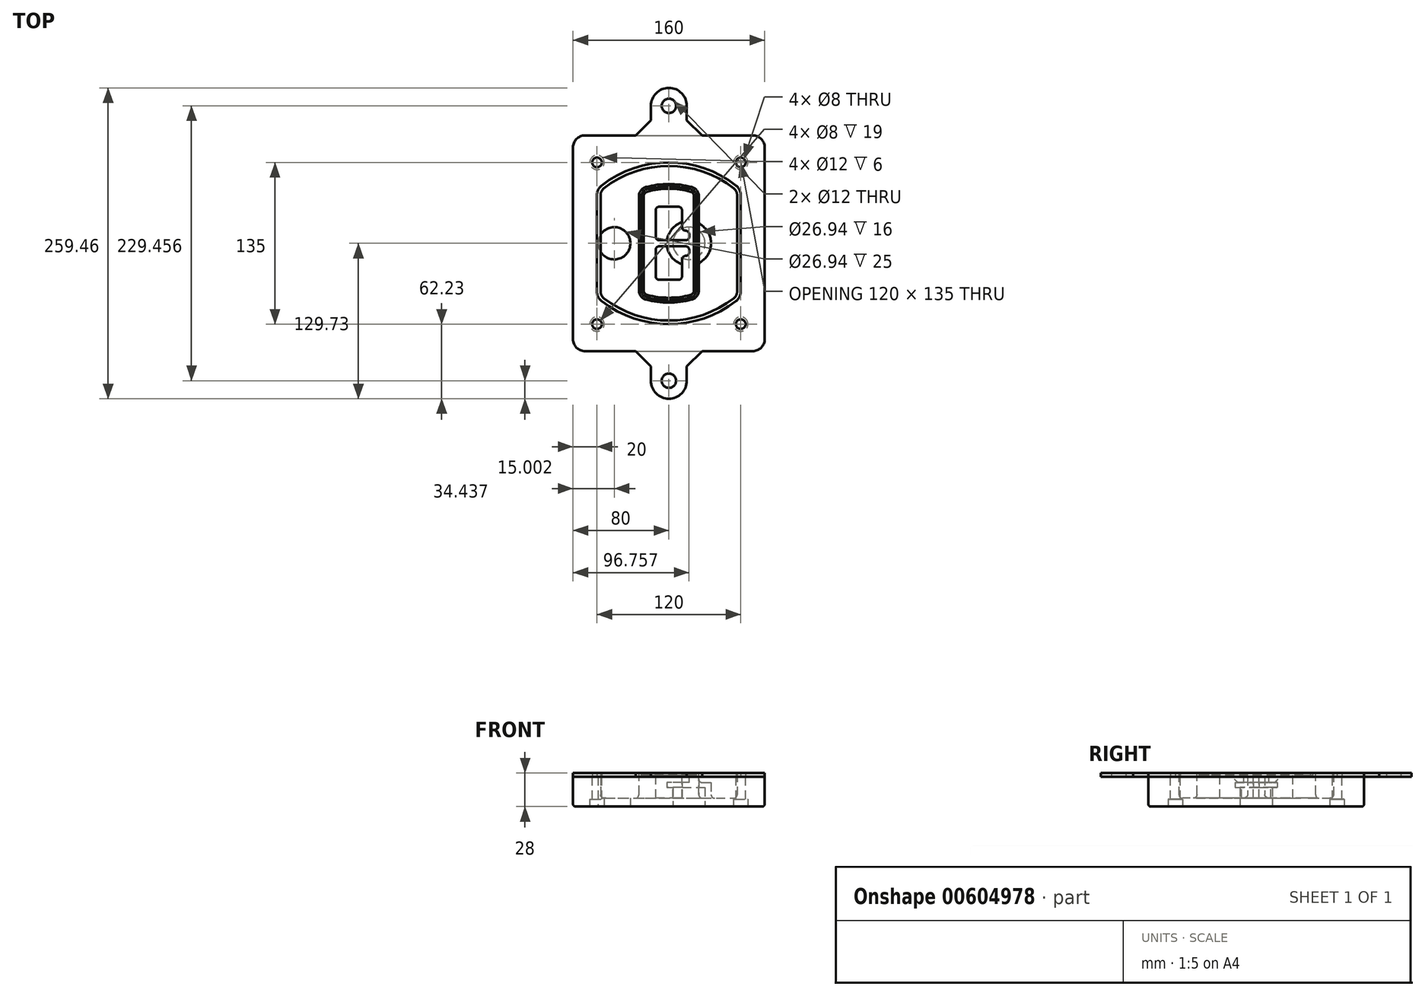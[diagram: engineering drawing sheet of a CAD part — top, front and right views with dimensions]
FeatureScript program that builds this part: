
annotation { "Feature Type Name" : "Feature", "Feature Type Description" : "" }
export const myFeature = defineFeature(function(context is Context, id is Id, definition is map)
    precondition{}
    {
        {
            var Q0;
            Q0=qCreatedBy(makeId("Top.planeOp"),FACE);
            var sketch = newSketch(context, id + "F0", { "sketchPlane" : qUnion([Q0])});
            skPoint(sketch, "E0.rect.middle", {"position": v(0, 0) * mm});
            skLineSegment(sketch, "E1.bottom", {"start": v(-70, -90) * mm, "end": v(70, -90) * mm});
            skLineSegment(sketch, "E1.top", {"start": v(-70, 90) * mm, "end": v(70, 90) * mm});
            skLineSegment(sketch, "E1.left", {"start": v(-80, -80) * mm, "end": v(-80, 80) * mm});
            skLineSegment(sketch, "E1.right", {"start": v(80, -80) * mm, "end": v(80, 80) * mm});
            skLineSegment(sketch, "E2", {"start": v(-80, 90) * mm, "end": v(80, -90) * mm, "construction": true});
            skLineSegment(sketch, "E3", {"start": v(80, 90) * mm, "end": v(-80, -90) * mm, "construction": true});
            skCircle(sketch, "E4", {"center": v(-60, 67.5) * mm, "radius": 4 * mm});
            skCircle(sketch, "E5", {"center": v(60, 67.5) * mm, "radius": 4 * mm});
            skCircle(sketch, "E6", {"center": v(60, -67.5) * mm, "radius": 4 * mm});
            skCircle(sketch, "E7", {"center": v(-60, -67.5) * mm, "radius": 4 * mm});
            skLineSegment(sketch, "E8", {"start": v(-60, 67.5) * mm, "end": v(60, 67.5) * mm, "construction": true});
            skLineSegment(sketch, "E9", {"start": v(60, 67.5) * mm, "end": v(60, -67.5) * mm, "construction": true});
            skLineSegment(sketch, "E10", {"start": v(60, -67.5) * mm, "end": v(-60, -67.5) * mm, "construction": true});
            skLineSegment(sketch, "E11", {"start": v(-60, -67.5) * mm, "end": v(-60, 67.5) * mm, "construction": true});
            skLineSegment(sketch, "E12", {"start": v(-60, 40.3) * mm, "end": v(-60, -40.3) * mm});
            skLineSegment(sketch, "E13", {"start": v(60, 40.3) * mm, "end": v(60, -40.3) * mm});
            skArc(sketch, "E14", {"start": v(56.15, 48.18) * mm, "mid": v(0, 67.5) * mm, "end": v(-56.15, 48.18) * mm});
            skArc(sketch, "E15", {"start": v(-56.15, -48.18) * mm, "mid": v(0, -67.5) * mm, "end": v(56.15, -48.18) * mm});
            skLineSegment(sketch, "E16", {"start": v(-60, 0) * mm, "end": v(60, 0) * mm, "construction": true});
            skPoint(sketch, "E17.visualSharp", {"position": v(-60, -45) * mm});
            skArc(sketch, "E17.filletArc", {"start": v(-60, -40.3) * mm, "mid": v(-58.99, -44.68) * mm, "end": v(-56.15, -48.18) * mm});
            skPoint(sketch, "E18.visualSharp", {"position": v(-60, 45) * mm});
            skArc(sketch, "E18.filletArc", {"start": v(-56.15, 48.18) * mm, "mid": v(-58.99, 44.68) * mm, "end": v(-60, 40.3) * mm});
            skPoint(sketch, "E19.visualSharp", {"position": v(60, 45) * mm});
            skArc(sketch, "E19.filletArc", {"start": v(60, 40.3) * mm, "mid": v(58.99, 44.68) * mm, "end": v(56.15, 48.18) * mm});
            skPoint(sketch, "E20.visualSharp", {"position": v(60, -45) * mm});
            skArc(sketch, "E20.filletArc", {"start": v(56.15, -48.18) * mm, "mid": v(58.99, -44.68) * mm, "end": v(60, -40.3) * mm});
            skPoint(sketch, "E21.visualSharp", {"position": v(-80, 90) * mm});
            skArc(sketch, "E21.filletArc", {"start": v(-70, 90) * mm, "mid": v(-77.07, 87.07) * mm, "end": v(-80, 80) * mm});
            skPoint(sketch, "E22.visualSharp", {"position": v(80, 90) * mm});
            skArc(sketch, "E22.filletArc", {"start": v(80, 80) * mm, "mid": v(77.07, 87.07) * mm, "end": v(70, 90) * mm});
            skPoint(sketch, "E23.visualSharp", {"position": v(80, -90) * mm});
            skArc(sketch, "E23.filletArc", {"start": v(70, -90) * mm, "mid": v(77.07, -87.07) * mm, "end": v(80, -80) * mm});
            skPoint(sketch, "E24.visualSharp", {"position": v(-80, -90) * mm});
            skArc(sketch, "E24.filletArc", {"start": v(-80, -80) * mm, "mid": v(-77.07, -87.07) * mm, "end": v(-70, -90) * mm});
            skArc(sketch, "E25.0", {"start": v(57, 40.3) * mm, "mid": v(56.3, 43.36) * mm, "end": v(54.3, 45.81) * mm});
            skLineSegment(sketch, "E25.1", {"start": v(57, 40.3) * mm, "end": v(57, -40.3) * mm});
            skArc(sketch, "E25.2", {"start": v(54.3, -45.81) * mm, "mid": v(56.3, -43.36) * mm, "end": v(57, -40.3) * mm});
            skArc(sketch, "E25.3", {"start": v(-54.3, -45.81) * mm, "mid": v(0, -64.5) * mm, "end": v(54.3, -45.81) * mm});
            skArc(sketch, "E25.4", {"start": v(-57, -40.3) * mm, "mid": v(-56.3, -43.36) * mm, "end": v(-54.3, -45.81) * mm});
            skArc(sketch, "E25.5", {"start": v(54.3, 45.81) * mm, "mid": v(0, 64.5) * mm, "end": v(-54.3, 45.81) * mm});
            skLineSegment(sketch, "E25.6", {"start": v(-57, 40.3) * mm, "end": v(-57, -40.3) * mm});
            skArc(sketch, "E25.7", {"start": v(-54.3, 45.81) * mm, "mid": v(-56.3, 43.36) * mm, "end": v(-57, 40.3) * mm});
            skArc(sketch, "E26.0", {"start": v(-58.62, 51.33) * mm, "mid": v(-62.58, 46.43) * mm, "end": v(-64, 40.3) * mm});
            skArc(sketch, "E26.1", {"start": v(58.62, 51.33) * mm, "mid": v(0, 71.5) * mm, "end": v(-58.62, 51.33) * mm});
            skArc(sketch, "E26.2", {"start": v(64, 40.3) * mm, "mid": v(62.58, 46.43) * mm, "end": v(58.62, 51.33) * mm});
            skLineSegment(sketch, "E26.3", {"start": v(64, 40.3) * mm, "end": v(64, -40.3) * mm});
            skArc(sketch, "E26.4", {"start": v(58.62, -51.33) * mm, "mid": v(62.58, -46.43) * mm, "end": v(64, -40.3) * mm});
            skLineSegment(sketch, "E26.5", {"start": v(-64, 40.3) * mm, "end": v(-64, -40.3) * mm});
            skArc(sketch, "E26.6", {"start": v(-58.62, -51.33) * mm, "mid": v(0, -71.5) * mm, "end": v(58.62, -51.33) * mm});
            skArc(sketch, "E26.7", {"start": v(-64, -40.3) * mm, "mid": v(-62.58, -46.43) * mm, "end": v(-58.62, -51.33) * mm});
            skSolve(sketch);
        }
        {
            var Q0;
            Q0=makeQuery(id+"F0.imprint","IMPRINT",FACE,{"disambiguationData":[TD([[makeQuery(id+"F0.imprint","IMPRINT",EDGE,{"derivedFrom":sQuery(id+"F0.wireOp",EDGE,"E1.bottom")}),1.0]])]});
            var Q1;
            Q1=makeQuery(id+"F0.imprint","IMPRINT",FACE,{"disambiguationData":[TD([[makeQuery(id+"F0.imprint","IMPRINT",EDGE,{"derivedFrom":sQuery(id+"F0.wireOp",EDGE,"E12")}),1.0]])]});
            var Q2;
            Q2=makeQuery(id+"F0.imprint","IMPRINT",FACE,{"disambiguationData":[TD([[makeQuery(id+"F0.imprint","IMPRINT",EDGE,{"derivedFrom":sQuery(id+"F0.wireOp",EDGE,"E25.0")}),1.0]])]});
            var Q3;
            Q3=makeQuery(id+"F0.imprint","IMPRINT",FACE,{"disambiguationData":[TD([[makeQuery(id+"F0.imprint","IMPRINT",EDGE,{"derivedFrom":sQuery(id+"F0.wireOp",EDGE,"E12")}),-1.0]])]});
            extrude(context, id + "F1", {"entities" : qUnion([Q0, Q1, Q2, Q3]), "oppositeDirection" : true, "depth" : 25 * mm});
        }
        {
            var Q0;
            Q0=makeQuery(id+"F0.imprint","IMPRINT",FACE,{"disambiguationData":[TD([[makeQuery(id+"F0.imprint","IMPRINT",EDGE,{"derivedFrom":sQuery(id+"F0.wireOp",EDGE,"E12")}),1.0]])]});
            extrude(context, id + "F2", {"entities" : qUnion([Q0]), "operationType" : NewBodyOperationType.ADD, "depth" : 3 * mm});
        }
        {
            var Q0;
            Q0=makeQuery(id+"F0.imprint","IMPRINT",FACE,{"disambiguationData":[TD([[makeQuery(id+"F0.imprint","IMPRINT",EDGE,{"derivedFrom":sQuery(id+"F0.wireOp",EDGE,"E25.0")}),1.0]])]});
            extrude(context, id + "F3", {"entities" : qUnion([Q0]), "operationType" : NewBodyOperationType.REMOVE, "oppositeDirection" : true, "depth" : 18 * mm});
        }
        {
            var Q0;
            Q0=makeQuery(id+"F2.opExtrude","CAP_FACE",FACE,{"disambiguationData":[OSD([sQuery(id+"F0.wireOp",EDGE,"E12"),sQuery(id+"F0.wireOp",EDGE,"E13"),sQuery(id+"F0.wireOp",EDGE,"E14"),sQuery(id+"F0.wireOp",EDGE,"E15"),sQuery(id+"F0.wireOp",EDGE,"E17.filletArc"),sQuery(id+"F0.wireOp",EDGE,"E18.filletArc"),sQuery(id+"F0.wireOp",EDGE,"E19.filletArc"),sQuery(id+"F0.wireOp",EDGE,"E20.filletArc"),sQuery(id+"F0.wireOp",EDGE,"E25.0"),sQuery(id+"F0.wireOp",EDGE,"E25.1"),sQuery(id+"F0.wireOp",EDGE,"E25.2"),sQuery(id+"F0.wireOp",EDGE,"E25.3"),sQuery(id+"F0.wireOp",EDGE,"E25.4"),sQuery(id+"F0.wireOp",EDGE,"E25.5"),sQuery(id+"F0.wireOp",EDGE,"E25.6"),sQuery(id+"F0.wireOp",EDGE,"E25.7")])],"isStart":false});
            var sketch = newSketch(context, id + "F4", { "sketchPlane" : qUnion([Q0])});
            skArc(sketch, "E27.0", {"start": v(-19.08, -46.97) * mm, "mid": v(0, -49.5) * mm, "end": v(19.08, -46.97) * mm});
            skArc(sketch, "E28.0", {"start": v(19.08, 46.97) * mm, "mid": v(0, 49.5) * mm, "end": v(-19.08, 46.97) * mm});
            skLineSegment(sketch, "E29", {"start": v(-25, 39.25) * mm, "end": v(-25, -39.25) * mm});
            skLineSegment(sketch, "E30", {"start": v(25, 39.25) * mm, "end": v(25, -39.25) * mm});
            skLineSegment(sketch, "E31", {"start": v(-25, 45.1) * mm, "end": v(25, 45.1) * mm, "construction": true});
            skLineSegment(sketch, "E32", {"start": v(-25, -45.1) * mm, "end": v(25, -45.1) * mm, "construction": true});
            skPoint(sketch, "E33.visualSharp", {"position": v(-25, 45.1) * mm});
            skArc(sketch, "E33.filletArc", {"start": v(-19.08, 46.97) * mm, "mid": v(-23.35, 44.11) * mm, "end": v(-25, 39.25) * mm});
            skPoint(sketch, "E34.visualSharp", {"position": v(25, 45.1) * mm});
            skArc(sketch, "E34.filletArc", {"start": v(25, 39.25) * mm, "mid": v(23.35, 44.11) * mm, "end": v(19.08, 46.97) * mm});
            skPoint(sketch, "E35.visualSharp", {"position": v(25, -45.1) * mm});
            skArc(sketch, "E35.filletArc", {"start": v(19.08, -46.97) * mm, "mid": v(23.35, -44.11) * mm, "end": v(25, -39.25) * mm});
            skPoint(sketch, "E36.visualSharp", {"position": v(-25, -45.1) * mm});
            skArc(sketch, "E36.filletArc", {"start": v(-25, -39.25) * mm, "mid": v(-23.35, -44.11) * mm, "end": v(-19.08, -46.97) * mm});
            skArc(sketch, "E37.0", {"start": v(54.3, 45.81) * mm, "mid": v(0, 64.5) * mm, "end": v(-54.3, 45.81) * mm});
            skArc(sketch, "E37.1", {"start": v(-54.3, 45.81) * mm, "mid": v(-56.3, 43.36) * mm, "end": v(-57, 40.3) * mm});
            skLineSegment(sketch, "E37.2", {"start": v(-57, 40.3) * mm, "end": v(-57, -40.3) * mm});
            skArc(sketch, "E37.3", {"start": v(-57, -40.3) * mm, "mid": v(-56.3, -43.36) * mm, "end": v(-54.3, -45.81) * mm});
            skArc(sketch, "E37.4", {"start": v(-54.3, -45.81) * mm, "mid": v(0, -64.5) * mm, "end": v(54.3, -45.81) * mm});
            skArc(sketch, "E37.5", {"start": v(54.3, -45.81) * mm, "mid": v(56.3, -43.36) * mm, "end": v(57, -40.3) * mm});
            skLineSegment(sketch, "E37.6", {"start": v(57, 40.3) * mm, "end": v(57, -40.3) * mm});
            skArc(sketch, "E37.7", {"start": v(57, 40.3) * mm, "mid": v(56.3, 43.36) * mm, "end": v(54.3, 45.81) * mm});
            skLineSegment(sketch, "E38.0", {"start": v(23, 39.25) * mm, "end": v(23, -39.25) * mm});
            skArc(sketch, "E38.1", {"start": v(18.56, -45.04) * mm, "mid": v(21.76, -42.9) * mm, "end": v(23, -39.25) * mm});
            skArc(sketch, "E38.2", {"start": v(-18.56, -45.04) * mm, "mid": v(0, -47.5) * mm, "end": v(18.56, -45.04) * mm});
            skArc(sketch, "E38.3", {"start": v(-23, -39.25) * mm, "mid": v(-21.76, -42.9) * mm, "end": v(-18.56, -45.04) * mm});
            skLineSegment(sketch, "E38.4", {"start": v(-23, 39.25) * mm, "end": v(-23, -39.25) * mm});
            skArc(sketch, "E38.5", {"start": v(23, 39.25) * mm, "mid": v(21.76, 42.9) * mm, "end": v(18.56, 45.04) * mm});
            skArc(sketch, "E38.6", {"start": v(-18.56, 45.04) * mm, "mid": v(-21.76, 42.9) * mm, "end": v(-23, 39.25) * mm});
            skArc(sketch, "E38.7", {"start": v(18.56, 45.04) * mm, "mid": v(0, 47.5) * mm, "end": v(-18.56, 45.04) * mm});
            skArc(sketch, "E39.0", {"start": v(21, 39.25) * mm, "mid": v(20.18, 41.68) * mm, "end": v(18.04, 43.1) * mm});
            skLineSegment(sketch, "E39.1", {"start": v(21, 39.25) * mm, "end": v(21, -39.25) * mm});
            skArc(sketch, "E39.2", {"start": v(18.04, -43.1) * mm, "mid": v(20.18, -41.68) * mm, "end": v(21, -39.25) * mm});
            skArc(sketch, "E39.3", {"start": v(-18.04, -43.1) * mm, "mid": v(0, -45.5) * mm, "end": v(18.04, -43.1) * mm});
            skArc(sketch, "E39.4", {"start": v(-21, -39.25) * mm, "mid": v(-20.18, -41.68) * mm, "end": v(-18.04, -43.1) * mm});
            skArc(sketch, "E39.5", {"start": v(18.04, 43.1) * mm, "mid": v(0, 45.5) * mm, "end": v(-18.04, 43.1) * mm});
            skLineSegment(sketch, "E39.6", {"start": v(-21, 39.25) * mm, "end": v(-21, -39.25) * mm});
            skArc(sketch, "E39.7", {"start": v(-18.04, 43.1) * mm, "mid": v(-20.18, 41.68) * mm, "end": v(-21, 39.25) * mm});
            skLineSegment(sketch, "E40", {"start": v(-25, 0) * mm, "end": v(25, 0) * mm, "construction": true});
            skLineSegment(sketch, "E41", {"start": v(-11, 5.5) * mm, "end": v(-11, 27.5) * mm});
            skLineSegment(sketch, "E42", {"start": v(-8, 30.5) * mm, "end": v(8, 30.5) * mm});
            skLineSegment(sketch, "E43", {"start": v(11, 27.5) * mm, "end": v(11, 13.5) * mm});
            skLineSegment(sketch, "E44", {"start": v(14, 10.5) * mm, "end": v(14, 10.5) * mm});
            skLineSegment(sketch, "E45", {"start": v(17, 7.5) * mm, "end": v(17, 5.5) * mm});
            skLineSegment(sketch, "E46", {"start": v(14, 2.5) * mm, "end": v(-8, 2.5) * mm});
            skPoint(sketch, "E47.visualSharp", {"position": v(-11, 30.5) * mm});
            skArc(sketch, "E47.filletArc", {"start": v(-8, 30.5) * mm, "mid": v(-10.12, 29.62) * mm, "end": v(-11, 27.5) * mm});
            skPoint(sketch, "E48.visualSharp", {"position": v(11, 30.5) * mm});
            skArc(sketch, "E48.filletArc", {"start": v(11, 27.5) * mm, "mid": v(10.12, 29.62) * mm, "end": v(8, 30.5) * mm});
            skPoint(sketch, "E49.visualSharp", {"position": v(11, 10.5) * mm});
            skArc(sketch, "E49.filletArc", {"start": v(11, 13.5) * mm, "mid": v(11.88, 11.38) * mm, "end": v(14, 10.5) * mm});
            skPoint(sketch, "E50.visualSharp", {"position": v(17, 10.5) * mm});
            skArc(sketch, "E50.filletArc", {"start": v(17, 7.5) * mm, "mid": v(16.12, 9.62) * mm, "end": v(14, 10.5) * mm});
            skPoint(sketch, "E51.visualSharp", {"position": v(17, 2.5) * mm});
            skArc(sketch, "E51.filletArc", {"start": v(14, 2.5) * mm, "mid": v(16.12, 3.38) * mm, "end": v(17, 5.5) * mm});
            skPoint(sketch, "E52.visualSharp", {"position": v(-11, 2.5) * mm});
            skArc(sketch, "E52.filletArc", {"start": v(-11, 5.5) * mm, "mid": v(-10.12, 3.38) * mm, "end": v(-8, 2.5) * mm});
            skLineSegment(sketch, "E53.0.MirrorCS", {"start": v(14, -2.5) * mm, "end": v(-8, -2.5) * mm});
            skArc(sketch, "E54.0.MirrorCS", {"start": v(-11, -5.5) * mm, "mid": v(-10.12, -3.38) * mm, "end": v(-8, -2.5) * mm});
            skLineSegment(sketch, "E55.0.MirrorCS", {"start": v(-11, -5.5) * mm, "end": v(-11, -27.5) * mm});
            skArc(sketch, "E56.0.MirrorCS", {"start": v(-8, -30.5) * mm, "mid": v(-10.12, -29.62) * mm, "end": v(-11, -27.5) * mm});
            skLineSegment(sketch, "E57.0.MirrorCS", {"start": v(-8, -30.5) * mm, "end": v(8, -30.5) * mm});
            skArc(sketch, "E58.0.MirrorCS", {"start": v(11, -27.5) * mm, "mid": v(10.12, -29.62) * mm, "end": v(8, -30.5) * mm});
            skLineSegment(sketch, "E59.0.MirrorCS", {"start": v(11, -27.5) * mm, "end": v(11, -13.5) * mm});
            skArc(sketch, "E60.0.MirrorCS", {"start": v(11, -13.5) * mm, "mid": v(11.88, -11.38) * mm, "end": v(14, -10.5) * mm});
            skArc(sketch, "E61.0.MirrorCS", {"start": v(17, -7.5) * mm, "mid": v(16.12, -9.62) * mm, "end": v(14, -10.5) * mm});
            skLineSegment(sketch, "E62.0.MirrorCS", {"start": v(17, -7.5) * mm, "end": v(17, -5.5) * mm});
            skArc(sketch, "E63.0.MirrorCS", {"start": v(14, -2.5) * mm, "mid": v(16.12, -3.38) * mm, "end": v(17, -5.5) * mm});
            skSolve(sketch);
        }
        {
            var Q0;
            Q0=makeQuery(id+"F4.imprint","IMPRINT",FACE,{"disambiguationData":[TD([[makeQuery(id+"F4.imprint","IMPRINT",EDGE,{"derivedFrom":sQuery(id+"F4.wireOp",EDGE,"E27.0")}),1.0]])]});
            var Q1;
            Q1=makeQuery(id+"F4.imprint","IMPRINT",FACE,{"disambiguationData":[TD([[makeQuery(id+"F4.imprint","IMPRINT",EDGE,{"derivedFrom":sQuery(id+"F4.wireOp",EDGE,"E38.0")}),-1.0]])]});
            var Q2;
            Q2=makeQuery(id+"F4.imprint","IMPRINT",FACE,{"disambiguationData":[TD([[makeQuery(id+"F4.imprint","IMPRINT",EDGE,{"derivedFrom":sQuery(id+"F4.wireOp",EDGE,"E39.0")}),1.0]])]});
            extrude(context, id + "F5", {"entities" : qUnion([Q0, Q1, Q2]), "operationType" : NewBodyOperationType.ADD, "endBound" : BoundingType.UP_TO_NEXT, "oppositeDirection" : true, "depth" : 25 * mm});
        }
        {
            var Q0;
            Q0=makeQuery(id+"F4.imprint","IMPRINT",FACE,{"disambiguationData":[TD([[makeQuery(id+"F4.imprint","IMPRINT",EDGE,{"derivedFrom":sQuery(id+"F4.wireOp",EDGE,"E38.0")}),-1.0]])]});
            extrude(context, id + "F6", {"entities" : qUnion([Q0]), "operationType" : NewBodyOperationType.REMOVE, "oppositeDirection" : true, "depth" : 2 * mm});
        }
        {
            var Q0;
            Q0=makeQuery(id+"F1.opExtrude","CAP_FACE",FACE,{"disambiguationData":[OSD([sQuery(id+"F0.wireOp",EDGE,"E1.bottom"),sQuery(id+"F0.wireOp",EDGE,"E1.top"),sQuery(id+"F0.wireOp",EDGE,"E1.left"),sQuery(id+"F0.wireOp",EDGE,"E1.right"),sQuery(id+"F0.wireOp",EDGE,"E4"),sQuery(id+"F0.wireOp",EDGE,"E5"),sQuery(id+"F0.wireOp",EDGE,"E6"),sQuery(id+"F0.wireOp",EDGE,"E7"),sQuery(id+"F0.wireOp",EDGE,"E21.filletArc"),sQuery(id+"F0.wireOp",EDGE,"E22.filletArc"),sQuery(id+"F0.wireOp",EDGE,"E23.filletArc"),sQuery(id+"F0.wireOp",EDGE,"E24.filletArc")])],"isStart":false});
            var sketch = newSketch(context, id + "F7", { "sketchPlane" : qUnion([Q0])});
            skCircle(sketch, "E64", {"center": v(16.76, 0) * mm, "radius": 13.47 * mm});
            skCircle(sketch, "E65", {"center": v(-45.56, 0) * mm, "radius": 13.47 * mm});
            skLineSegment(sketch, "E66", {"start": v(80, 0) * mm, "end": v(-80, 0) * mm});
            skCircle(sketch, "E67", {"center": v(16.76, 0) * mm, "radius": 18.47 * mm});
            skCircle(sketch, "E68", {"center": v(60, -67.5) * mm, "radius": 6 * mm});
            skCircle(sketch, "E69", {"center": v(-60, -67.5) * mm, "radius": 6 * mm});
            skCircle(sketch, "E70", {"center": v(-60, 67.5) * mm, "radius": 6 * mm});
            skCircle(sketch, "E71", {"center": v(60, 67.5) * mm, "radius": 6 * mm});
            skSolve(sketch);
        }
        {
            var Q0;
            {var subQ1=sQuery(id+"F7.wireOp",EDGE,"E66");var subQ4=sQuery(id+"F7.wireOp",EDGE,"E64");var subQ6=makeQuery(id+"F7.imprint","INTERSECT",VERTEX,{"disambiguationData":[OD(0.0)],"derivedFrom":[subQ4,subQ1]});Q0=makeQuery(id+"F7.imprint","IMPRINT",FACE,{"disambiguationData":[TD([[makeQuery(id+"F7.imprint","IMPRINT",EDGE,{"disambiguationData":[TD([[subQ6,-1.0]])],"derivedFrom":subQ4}),-1.0]])]});}
            var Q1;
            {var subQ0=sQuery(id+"F7.wireOp",EDGE,"E66");var subQ1=sQuery(id+"F7.wireOp",EDGE,"E64");var subQ3=makeQuery(id+"F7.imprint","INTERSECT",VERTEX,{"disambiguationData":[OD(0.0)],"derivedFrom":[subQ1,subQ0]});Q1=makeQuery(id+"F7.imprint","IMPRINT",FACE,{"disambiguationData":[TD([[makeQuery(id+"F7.imprint","IMPRINT",EDGE,{"disambiguationData":[TD([[subQ3,-1.0]])],"derivedFrom":subQ1}),1.0]])]});}
            var Q2;
            {var subQ0=sQuery(id+"F7.wireOp",EDGE,"E66");var subQ1=sQuery(id+"F7.wireOp",EDGE,"E64");var subQ3=makeQuery(id+"F7.imprint","INTERSECT",VERTEX,{"disambiguationData":[OD(0.0)],"derivedFrom":[subQ1,subQ0]});Q2=makeQuery(id+"F7.imprint","IMPRINT",FACE,{"disambiguationData":[TD([[makeQuery(id+"F7.imprint","IMPRINT",EDGE,{"disambiguationData":[TD([[subQ3,1.0]])],"derivedFrom":subQ1}),1.0]])]});}
            var Q3;
            {var subQ1=sQuery(id+"F7.wireOp",EDGE,"E66");var subQ4=sQuery(id+"F7.wireOp",EDGE,"E64");var subQ6=makeQuery(id+"F7.imprint","INTERSECT",VERTEX,{"disambiguationData":[OD(0.0)],"derivedFrom":[subQ4,subQ1]});Q3=makeQuery(id+"F7.imprint","IMPRINT",FACE,{"disambiguationData":[TD([[makeQuery(id+"F7.imprint","IMPRINT",EDGE,{"disambiguationData":[TD([[subQ6,1.0]])],"derivedFrom":subQ4}),-1.0]])]});}
            extrude(context, id + "F8", {"entities" : qUnion([Q0, Q1, Q2, Q3]), "operationType" : NewBodyOperationType.ADD, "oppositeDirection" : true, "depth" : 20 * mm});
        }
        {
            var Q0;
            {var subQ0=sQuery(id+"F7.wireOp",EDGE,"E66");var subQ1=sQuery(id+"F7.wireOp",EDGE,"E64");var subQ3=makeQuery(id+"F7.imprint","INTERSECT",VERTEX,{"disambiguationData":[OD(0.0)],"derivedFrom":[subQ1,subQ0]});Q0=makeQuery(id+"F7.imprint","IMPRINT",FACE,{"disambiguationData":[TD([[makeQuery(id+"F7.imprint","IMPRINT",EDGE,{"disambiguationData":[TD([[subQ3,-1.0]])],"derivedFrom":subQ1}),1.0]])]});}
            var Q1;
            {var subQ0=sQuery(id+"F7.wireOp",EDGE,"E66");var subQ1=sQuery(id+"F7.wireOp",EDGE,"E64");var subQ3=makeQuery(id+"F7.imprint","INTERSECT",VERTEX,{"disambiguationData":[OD(0.0)],"derivedFrom":[subQ1,subQ0]});Q1=makeQuery(id+"F7.imprint","IMPRINT",FACE,{"disambiguationData":[TD([[makeQuery(id+"F7.imprint","IMPRINT",EDGE,{"disambiguationData":[TD([[subQ3,1.0]])],"derivedFrom":subQ1}),1.0]])]});}
            extrude(context, id + "F9", {"entities" : qUnion([Q0, Q1]), "operationType" : NewBodyOperationType.REMOVE, "oppositeDirection" : true, "depth" : 16 * mm});
        }
        {
            var Q0;
            {var subQ0=sQuery(id+"F7.wireOp",EDGE,"E66");var subQ1=sQuery(id+"F7.wireOp",EDGE,"E65");var subQ3=makeQuery(id+"F7.imprint","INTERSECT",VERTEX,{"disambiguationData":[OD(0.0)],"derivedFrom":[subQ1,subQ0]});Q0=makeQuery(id+"F7.imprint","IMPRINT",FACE,{"disambiguationData":[TD([[makeQuery(id+"F7.imprint","IMPRINT",EDGE,{"disambiguationData":[TD([[subQ3,-1.0]])],"derivedFrom":subQ1}),1.0]])]});}
            var Q1;
            {var subQ0=sQuery(id+"F7.wireOp",EDGE,"E66");var subQ1=sQuery(id+"F7.wireOp",EDGE,"E65");var subQ3=makeQuery(id+"F7.imprint","INTERSECT",VERTEX,{"disambiguationData":[OD(0.0)],"derivedFrom":[subQ1,subQ0]});Q1=makeQuery(id+"F7.imprint","IMPRINT",FACE,{"disambiguationData":[TD([[makeQuery(id+"F7.imprint","IMPRINT",EDGE,{"disambiguationData":[TD([[subQ3,1.0]])],"derivedFrom":subQ1}),1.0]])]});}
            extrude(context, id + "F10", {"entities" : qUnion([Q0, Q1]), "operationType" : NewBodyOperationType.REMOVE, "oppositeDirection" : true, "depth" : 25 * mm});
        }
        {
            var Q0;
            Q0=makeQuery(id+"F7.imprint","IMPRINT",FACE,{"disambiguationData":[TD([[makeQuery(id+"F7.imprint","IMPRINT",EDGE,{"derivedFrom":sQuery(id+"F7.wireOp",EDGE,"E68")}),1.0]])]});
            var Q1;
            Q1=makeQuery(id+"F7.imprint","IMPRINT",FACE,{"disambiguationData":[TD([[makeQuery(id+"F7.imprint","IMPRINT",EDGE,{"derivedFrom":makeQuery(id+"F1.opExtrude","CAP_EDGE",EDGE,{"disambiguationData":[OSD([sQuery(id+"F0.wireOp",EDGE,"E5")])],"isStart":false})}),-1.0]])]});
            var Q2;
            Q2=makeQuery(id+"F7.imprint","IMPRINT",FACE,{"disambiguationData":[TD([[makeQuery(id+"F7.imprint","IMPRINT",EDGE,{"derivedFrom":sQuery(id+"F7.wireOp",EDGE,"E69")}),1.0]])]});
            var Q3;
            Q3=makeQuery(id+"F7.imprint","IMPRINT",FACE,{"disambiguationData":[TD([[makeQuery(id+"F7.imprint","IMPRINT",EDGE,{"derivedFrom":makeQuery(id+"F1.opExtrude","CAP_EDGE",EDGE,{"disambiguationData":[OSD([sQuery(id+"F0.wireOp",EDGE,"E4")])],"isStart":false})}),-1.0]])]});
            var Q4;
            Q4=makeQuery(id+"F7.imprint","IMPRINT",FACE,{"disambiguationData":[TD([[makeQuery(id+"F7.imprint","IMPRINT",EDGE,{"derivedFrom":sQuery(id+"F7.wireOp",EDGE,"E70")}),1.0]])]});
            var Q5;
            Q5=makeQuery(id+"F7.imprint","IMPRINT",FACE,{"disambiguationData":[TD([[makeQuery(id+"F7.imprint","IMPRINT",EDGE,{"derivedFrom":makeQuery(id+"F1.opExtrude","CAP_EDGE",EDGE,{"disambiguationData":[OSD([sQuery(id+"F0.wireOp",EDGE,"E7")])],"isStart":false})}),-1.0]])]});
            var Q6;
            Q6=makeQuery(id+"F7.imprint","IMPRINT",FACE,{"disambiguationData":[TD([[makeQuery(id+"F7.imprint","IMPRINT",EDGE,{"derivedFrom":sQuery(id+"F7.wireOp",EDGE,"E71")}),1.0]])]});
            var Q7;
            Q7=makeQuery(id+"F7.imprint","IMPRINT",FACE,{"disambiguationData":[TD([[makeQuery(id+"F7.imprint","IMPRINT",EDGE,{"derivedFrom":makeQuery(id+"F1.opExtrude","CAP_EDGE",EDGE,{"disambiguationData":[OSD([sQuery(id+"F0.wireOp",EDGE,"E6")])],"isStart":false})}),-1.0]])]});
            extrude(context, id + "F11", {"entities" : qUnion([Q0, Q1, Q2, Q3, Q4, Q5, Q6, Q7]), "operationType" : NewBodyOperationType.REMOVE, "oppositeDirection" : true, "depth" : 6 * mm});
        }
        {
            var Q0;
            Q0=makeQuery(id+"F9.boolean.opBoolean","COPY",FACE,{"derivedFrom":makeQuery(id+"F9.opExtrude","CAP_FACE",FACE,{"disambiguationData":[OSD([sQuery(id+"F7.wireOp",EDGE,"E64")])],"isStart":false})});
            var sketch = newSketch(context, id + "F12", { "sketchPlane" : qUnion([Q0])});
            skArc(sketch, "E72.0", {"start": v(11, 17.55) * mm, "mid": v(2.57, 11.82) * mm, "end": v(-1.54, 2.5) * mm});
            skArc(sketch, "E72.1", {"start": v(-1.54, -2.5) * mm, "mid": v(2.57, -11.82) * mm, "end": v(11, -17.55) * mm});
            skLineSegment(sketch, "E73", {"start": v(-1.54, -2.5) * mm, "end": v(14, -2.5) * mm});
            skLineSegment(sketch, "E74.0", {"start": v(14, 2.5) * mm, "end": v(-1.54, 2.5) * mm});
            skArc(sketch, "E74.1", {"start": v(14, 2.5) * mm, "mid": v(16.12, 3.38) * mm, "end": v(17, 5.5) * mm});
            skLineSegment(sketch, "E74.2", {"start": v(17, 7.5) * mm, "end": v(17, 5.5) * mm});
            skArc(sketch, "E74.3", {"start": v(17, 7.5) * mm, "mid": v(16.12, 9.62) * mm, "end": v(14, 10.5) * mm});
            skArc(sketch, "E74.4", {"start": v(11, 13.5) * mm, "mid": v(11.88, 11.38) * mm, "end": v(14, 10.5) * mm});
            skLineSegment(sketch, "E74.5", {"start": v(11, 17.55) * mm, "end": v(11, 13.5) * mm});
            skLineSegment(sketch, "E74.7", {"start": v(14, -2.5) * mm, "end": v(-1.54, -2.5) * mm});
            skArc(sketch, "E74.8", {"start": v(14, -2.5) * mm, "mid": v(16.12, -3.38) * mm, "end": v(17, -5.5) * mm});
            skLineSegment(sketch, "E74.9", {"start": v(17, -7.5) * mm, "end": v(17, -5.5) * mm});
            skArc(sketch, "E74.10", {"start": v(17, -7.5) * mm, "mid": v(16.12, -9.62) * mm, "end": v(14, -10.5) * mm});
            skArc(sketch, "E74.11", {"start": v(11, -13.5) * mm, "mid": v(11.88, -11.38) * mm, "end": v(14, -10.5) * mm});
            skLineSegment(sketch, "E74.12", {"start": v(11, -17.55) * mm, "end": v(11, -13.5) * mm});
            skPoint(sketch, "E75.orphan", {"position": v(11, -27.5) * mm});
            skPoint(sketch, "E76.orphan", {"position": v(-8, -2.5) * mm});
            skPoint(sketch, "E77.orphan", {"position": v(-8, 2.5) * mm});
            skPoint(sketch, "E78.orphan", {"position": v(11, 27.5) * mm});
            skSolve(sketch);
        }
        {
            var Q0;
            {var subQ7=sQuery(id+"F12.wireOp",EDGE,"E72.0");var subQ14=sQuery(id+"F12.wireOp",EDGE,"E72.1");var subQ16=sQuery(id+"F12.wireOp",EDGE,"E74.1");var subQ18=sQuery(id+"F12.wireOp",EDGE,"E74.8");Q0=qUnion([makeQuery(id+"F12.imprint","IMPRINT",FACE,{"disambiguationData":[TD([[makeQuery(id+"F12.imprint","IMPRINT",EDGE,{"derivedFrom":subQ7}),1.0]])]}),makeQuery(id+"F12.imprint","IMPRINT",FACE,{"disambiguationData":[TD([[makeQuery(id+"F12.imprint","IMPRINT",EDGE,{"derivedFrom":subQ14}),1.0]])]}),makeQuery(id+"F12.imprint","IMPRINT",FACE,{"disambiguationData":[TD([[makeQuery(id+"F12.imprint","IMPRINT",EDGE,{"derivedFrom":subQ16}),1.0]])]}),makeQuery(id+"F12.imprint","IMPRINT",FACE,{"disambiguationData":[TD([[makeQuery(id+"F12.imprint","IMPRINT",EDGE,{"derivedFrom":subQ18}),-1.0]])]})]);}
            var Q1;
            Q1=makeQuery(id+"F5.boolean.opBoolean","SPLIT",FACE,{"disambiguationData":[TD([makeQuery(id+"F5.opExtrude","SWEPT_FACE",FACE,{"disambiguationData":[OSD([sQuery(id+"F4.wireOp",EDGE,"E41")])]})])],"derivedFrom":makeQuery(id+"F3.boolean.opBoolean","COPY",FACE,{"derivedFrom":makeQuery(id+"F3.opExtrude","CAP_FACE",FACE,{"disambiguationData":[OSD([sQuery(id+"F0.wireOp",EDGE,"E25.0"),sQuery(id+"F0.wireOp",EDGE,"E25.1"),sQuery(id+"F0.wireOp",EDGE,"E25.2"),sQuery(id+"F0.wireOp",EDGE,"E25.3"),sQuery(id+"F0.wireOp",EDGE,"E25.4"),sQuery(id+"F0.wireOp",EDGE,"E25.5"),sQuery(id+"F0.wireOp",EDGE,"E25.6"),sQuery(id+"F0.wireOp",EDGE,"E25.7")])],"isStart":false})})});
            extrude(context, id + "F13", {"entities" : qUnion([Q0]), "operationType" : NewBodyOperationType.REMOVE, "endBound" : BoundingType.UP_TO_SURFACE, "endBoundEntityFace" : qUnion([Q1]), "depth" : 25 * mm});
        }
        {
            var Q0;
            Q0=makeQuery(id+"F3.boolean.opBoolean","COPY",EDGE,{"derivedFrom":makeQuery(id+"F3.opExtrude","CAP_EDGE",EDGE,{"disambiguationData":[OSD([sQuery(id+"F0.wireOp",EDGE,"E25.6")])],"isStart":false})});
            var Q1;
            Q1=makeQuery(id+"F8.boolean.opBoolean","INTERSECT",EDGE,{"derivedFrom":[makeQuery(id+"F5.opExtrude","SWEPT_FACE",FACE,{"disambiguationData":[OSD([sQuery(id+"F4.wireOp",EDGE,"E30")])]}),makeQuery(id+"F8.opExtrude","CAP_FACE",FACE,{"disambiguationData":[OSD([sQuery(id+"F7.wireOp",EDGE,"E67")])],"isStart":false})]});
            var Q2;
            Q2=makeQuery(id+"F8.boolean.opBoolean","INTERSECT",EDGE,{"disambiguationData":[OD(1.0)],"derivedFrom":[makeQuery(id+"F5.opExtrude","SWEPT_FACE",FACE,{"disambiguationData":[OSD([sQuery(id+"F4.wireOp",EDGE,"E30")])]}),makeQuery(id+"F8.opExtrude","SWEPT_FACE",FACE,{"disambiguationData":[OSD([sQuery(id+"F7.wireOp",EDGE,"E67")])]})]});
            var Q3;
            {var subQ0=sQuery(id+"F4.wireOp",EDGE,"E30");Q3=makeQuery(id+"F8.boolean.opBoolean","SPLIT",EDGE,{"disambiguationData":[TD([makeQuery(id+"F5.opExtrude","SWEPT_FACE",FACE,{"disambiguationData":[OSD([sQuery(id+"F4.wireOp",EDGE,"E35.filletArc")])]})])],"derivedFrom":makeQuery(id+"F5.opExtrude","CAP_EDGE",EDGE,{"disambiguationData":[OSD([subQ0])],"isStart":false})});}
            var Q4;
            {var subQ0=sQuery(id+"F0.wireOp",EDGE,"E25.7");var subQ1=sQuery(id+"F0.wireOp",EDGE,"E25.1");var subQ2=sQuery(id+"F0.wireOp",EDGE,"E25.6");var subQ3=sQuery(id+"F0.wireOp",EDGE,"E25.5");var subQ4=sQuery(id+"F0.wireOp",EDGE,"E25.4");var subQ5=sQuery(id+"F0.wireOp",EDGE,"E25.0");var subQ6=sQuery(id+"F0.wireOp",EDGE,"E25.2");var subQ7=sQuery(id+"F0.wireOp",EDGE,"E25.3");Q4=makeQuery(id+"F8.boolean.opBoolean","INTERSECT",EDGE,{"derivedFrom":[makeQuery(id+"F5.boolean.opBoolean","SPLIT",FACE,{"disambiguationData":[TD([makeQuery(id+"F2.opExtrude","SWEPT_FACE",FACE,{"disambiguationData":[OSD([subQ5])]})])],"derivedFrom":makeQuery(id+"F3.boolean.opBoolean","COPY",FACE,{"derivedFrom":makeQuery(id+"F3.opExtrude","CAP_FACE",FACE,{"disambiguationData":[OSD([subQ5,subQ1,subQ6,subQ7,subQ4,subQ3,subQ2,subQ0])],"isStart":false})})}),makeQuery(id+"F8.opExtrude","SWEPT_FACE",FACE,{"disambiguationData":[OSD([sQuery(id+"F7.wireOp",EDGE,"E67")])]})]});}
            var Q5;
            Q5=makeQuery(id+"F8.boolean.opBoolean","INTERSECT",EDGE,{"disambiguationData":[OD(0.0)],"derivedFrom":[makeQuery(id+"F5.opExtrude","SWEPT_FACE",FACE,{"disambiguationData":[OSD([sQuery(id+"F4.wireOp",EDGE,"E30")])]}),makeQuery(id+"F8.opExtrude","SWEPT_FACE",FACE,{"disambiguationData":[OSD([sQuery(id+"F7.wireOp",EDGE,"E67")])]})]});
            fillet(context, id + "F14", {"entities" : qUnion([Q0, Q1, Q2, Q3, Q4, Q5]), "radius" : 3 * mm, "tangentPropagation" : true, "allowEdgeOverflow" : false});
        }
        {
            var Q0;
            Q0=makeQuery(id+"F1.opExtrude","CAP_EDGE",EDGE,{"disambiguationData":[OSD([sQuery(id+"F0.wireOp",EDGE,"E1.bottom")])],"isStart":false});
            fillet(context, id + "F15", {"entities" : qUnion([Q0]), "radius" : 2 * mm, "tangentPropagation" : true, "allowEdgeOverflow" : false});
        }
        {
            var Q0;
            {var subQ0=sQuery(id+"F0.wireOp",EDGE,"E21.filletArc");var subQ1=sQuery(id+"F0.wireOp",EDGE,"E7");var subQ2=sQuery(id+"F0.wireOp",EDGE,"E6");var subQ3=sQuery(id+"F0.wireOp",EDGE,"E5");var subQ4=sQuery(id+"F0.wireOp",EDGE,"E4");var subQ5=sQuery(id+"F0.wireOp",EDGE,"E22.filletArc");var subQ6=sQuery(id+"F0.wireOp",EDGE,"E1.bottom");var subQ7=sQuery(id+"F0.wireOp",EDGE,"E1.right");var subQ8=sQuery(id+"F0.wireOp",EDGE,"E1.top");var subQ9=sQuery(id+"F0.wireOp",EDGE,"E1.left");var subQ10=sQuery(id+"F0.wireOp",EDGE,"E23.filletArc");var subQ11=sQuery(id+"F0.wireOp",EDGE,"E24.filletArc");Q0=makeQuery(id+"F2.boolean.opBoolean","SPLIT",FACE,{"disambiguationData":[TD([makeQuery(id+"F1.opExtrude","SWEPT_FACE",FACE,{"disambiguationData":[OSD([subQ6])]})])],"derivedFrom":makeQuery(id+"F1.opExtrude","CAP_FACE",FACE,{"disambiguationData":[OSD([subQ6,subQ8,subQ9,subQ7,subQ4,subQ3,subQ2,subQ1,subQ0,subQ5,subQ10,subQ11])],"isStart":true})});}
            var sketch = newSketch(context, id + "F16", { "sketchPlane" : qUnion([Q0])});
            skLineSegment(sketch, "E79", {"start": v(-27.73, 90) * mm, "end": v(-15, 102.73) * mm});
            skLineSegment(sketch, "E80", {"start": v(27.73, 90) * mm, "end": v(15, 102.73) * mm});
            skLineSegment(sketch, "E81", {"start": v(-15, 102.73) * mm, "end": v(-15, 114.73) * mm});
            skLineSegment(sketch, "E82", {"start": v(15, 102.73) * mm, "end": v(15, 114.73) * mm});
            skArc(sketch, "E83", {"start": v(0, 129.73) * mm, "mid": v(-10.6, 125.33) * mm, "end": v(-15, 114.73) * mm});
            skPoint(sketch, "E83.startSnap0", {"position": v(0, 90) * mm});
            skArc(sketch, "E84", {"start": v(15, 114.73) * mm, "mid": v(10.6, 125.33) * mm, "end": v(0, 129.73) * mm});
            skCircle(sketch, "E85", {"center": v(0, 114.73) * mm, "radius": 6 * mm});
            skLineSegment(sketch, "E86", {"start": v(-80, 0) * mm, "end": v(80, 0) * mm, "construction": true});
            skLineSegment(sketch, "E87.MirrorCS", {"start": v(27.73, -90) * mm, "end": v(15, -102.73) * mm});
            skLineSegment(sketch, "E88.MirrorCS", {"start": v(15, -102.73) * mm, "end": v(15, -114.73) * mm});
            skArc(sketch, "E89.MirrorCS", {"start": v(15, -114.73) * mm, "mid": v(10.6, -125.33) * mm, "end": v(0, -129.73) * mm});
            skArc(sketch, "E90.MirrorCS", {"start": v(0, -129.73) * mm, "mid": v(-10.6, -125.33) * mm, "end": v(-15, -114.73) * mm});
            skLineSegment(sketch, "E91.MirrorCS", {"start": v(-15, -102.73) * mm, "end": v(-15, -114.73) * mm});
            skLineSegment(sketch, "E92.MirrorCS", {"start": v(-27.73, -90) * mm, "end": v(-15, -102.73) * mm});
            skCircle(sketch, "E93.MirrorC", {"center": v(0, -114.73) * mm, "radius": 6 * mm});
            skSolve(sketch);
        }
        {
            var Q0;
            {var subQ1=sQuery(id+"F16.wireOp",EDGE,"E79");Q0=makeQuery(id+"F16.imprint","IMPRINT",FACE,{"disambiguationData":[TD([[makeQuery(id+"F16.imprint","IMPRINT",EDGE,{"derivedFrom":subQ1}),-1.0]])]});}
            var Q1;
            {var subQ0=sQuery(id+"F16.wireOp",EDGE,"E87.MirrorCS");Q1=makeQuery(id+"F16.imprint","IMPRINT",FACE,{"disambiguationData":[TD([[makeQuery(id+"F16.imprint","IMPRINT",EDGE,{"derivedFrom":subQ0}),-1.0]])]});}
            var Q2;
            Q2=makeQuery(id+"F16.imprint","IMPRINT",FACE,{"disambiguationData":[TD([[makeQuery(id+"F16.imprint","IMPRINT",EDGE,{"derivedFrom":makeQuery(id+"F1.opExtrude","CAP_EDGE",EDGE,{"disambiguationData":[OSD([sQuery(id+"F0.wireOp",EDGE,"E1.left")])],"isStart":true})}),-1.0]])]});
            var Q3;
            Q3=makeQuery(id+"F2.opExtrude","CAP_FACE",FACE,{"disambiguationData":[OSD([sQuery(id+"F0.wireOp",EDGE,"E12"),sQuery(id+"F0.wireOp",EDGE,"E13"),sQuery(id+"F0.wireOp",EDGE,"E14"),sQuery(id+"F0.wireOp",EDGE,"E15"),sQuery(id+"F0.wireOp",EDGE,"E17.filletArc"),sQuery(id+"F0.wireOp",EDGE,"E18.filletArc"),sQuery(id+"F0.wireOp",EDGE,"E19.filletArc"),sQuery(id+"F0.wireOp",EDGE,"E20.filletArc"),sQuery(id+"F0.wireOp",EDGE,"E25.0"),sQuery(id+"F0.wireOp",EDGE,"E25.1"),sQuery(id+"F0.wireOp",EDGE,"E25.2"),sQuery(id+"F0.wireOp",EDGE,"E25.3"),sQuery(id+"F0.wireOp",EDGE,"E25.4"),sQuery(id+"F0.wireOp",EDGE,"E25.5"),sQuery(id+"F0.wireOp",EDGE,"E25.6"),sQuery(id+"F0.wireOp",EDGE,"E25.7")])],"isStart":false});
            extrude(context, id + "F17", {"entities" : qUnion([Q0, Q1, Q2]), "endBound" : BoundingType.UP_TO_SURFACE, "depth" : 5 * mm, "endBoundEntityFace" : qUnion([Q3]), "offsetDistance" : 25 * mm});
        }
    });
